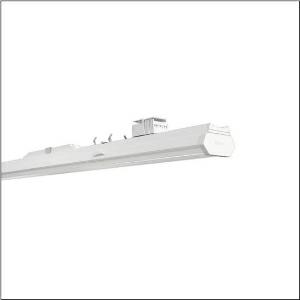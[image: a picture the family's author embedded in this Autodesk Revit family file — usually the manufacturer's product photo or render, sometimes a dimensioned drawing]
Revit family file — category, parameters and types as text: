
# Revit family: licross_r__11_protected_mo_51td117n485g_c933
name_source: partatom
category: Lighting Fixtures
units: mm (PartAtom-declared; Revit-internal decimal feet)

## family parameters
Cut with Voids When Loaded = No
Host = Face
Light Source = No
Part Type = Normal
Room Calculation Point = No
Round Connector Dimension = Use Diameter
Shared = No

## types (1)
- Licross® 11 Protected MO (1 x LED, 8680 lm, 48.6 W, 4000K)
    Apparent Load = 49 VA
    CIE Flux Codes = 83 94 98 100 100
    Color Rendering = 80
    Color Temperature = 4000K
    Default Elevation = 1800 mm
    Description = Licross® 11 Protected MO, luminaire insert, of sheet steel, galvanised, coil coated, white, length: 1.500mm, width: 90mm, height: 101mm, LED rated luminous flux: 8.680lm, light colour: 840, control gear: ON/OFF, with plug, 3-pole, with phase selection, mains connection: 220..240V, AC, 50/60Hz, rated input power: 49W, halogen-free wiring, primary light control with lens, of plastic, primary optical cover: cover, of PMMA, light emission: direct distribution, primary light characteristic: symmetric, protection rating (complete): IP54, insulation class (complete): insulation class I (protective earthing), certification: CE, ENEC, VDE, UKCA, protection symbol: D if used in an environment with non-conductive dust loads with corresponding accessories, impact resistance: IK06, permissible ambient temperature for indoor applications: -25..+35°C, corresponds to IFS (International Featured Standards) requirements for safety and quality in the food industry, reducing of maximum allowable ambient temperature of 5°C with ceiling mounting, LABS conformity tested according to VDMA 24364:2018-05, packaging unit: 1 piece
    Height = 92 mm
    Lamp = 1 x LED
    Lamp Light Flux = 8680 lm
    Lamp Power = 48.6 W
    Lamp count = 1
    Length = 1500 mm
    Luminous efficacy = 179 lm/W
    Manufacturer = Siteco
    ModVariant = No
    Model = 51TD117N485G
    Mounting Place = Ceiling
    Mounting Type = Pendant
    Number of Poles = 1
    OnlyDefault = Yes
    Power Factor = 1
    Product Name = Licross® 11 Protected MO
    Product group = luminaire insert
    ProductGroupID = 902
    Protection Class = Protection class I
    Protection Degree = IP 54
    RLX_Detail_Level = 1
    RLX_Emergency_Light_Flux = 0 lm
    RLX_Emergency_Type = 0
    RLX_Emergency_Type_DB = No
    RlxData = <blob elided: 20365 chars, md5=cf24656e>
    Socket = socket
    Standby Power = 0 W
    System Light Flux = 8680 lm
    System Power = 49 W
    Type Comments = Product without accessories
    Type Image = l_1256145.jpg
    URL = http://relux.com
    VarID = ---
    Voltage = 0 V
    Weight = 0.00 kg
    Width = 88 mm

## geometry (parser evidence)
native form markers: Blend x4, Sweep x11
no freeform markers — native parametric forms only
